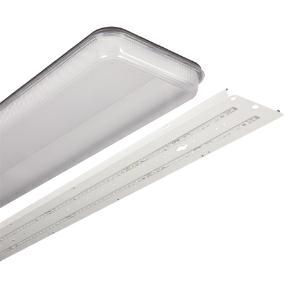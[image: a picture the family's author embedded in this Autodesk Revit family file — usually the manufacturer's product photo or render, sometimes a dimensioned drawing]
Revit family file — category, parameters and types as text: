
# Revit family: 3f_filippi_-_kit_led_retrofit_con_schermo_in_policarbonato_3f_filippi_-_a5027_-_kit_led_i3f_75__a3f_90___efdcafcb9e76d82e
name_source: partatom
category: Lighting Fixtures
units: mm (PartAtom-declared; Revit-internal decimal feet)

## family parameters
Cut with Voids When Loaded = No
Host = Face
Light Source = No
Part Type = Normal
Room Calculation Point = No
Round Connector Dimension = Use Diameter
Shared = No

## types (1)
- 3F Filippi - Kit LED Retrofit con schermo in policarbonato (1 x LED, 6996 lm, 49 W, 4000 K)
    Apparent Load = 49 VA
    Approval mark = ENEC
    CIE Flux Codes = 52 82 96 97 100
    Color Rendering = 80
    Color Temperature = 4000 K
    Control Gear = Electronic ballast
    Default Elevation = 1800 mm
    Description = Led retrofit kit suitable for Fluorescent Beta 2x i3F 75, A3F 90 and A3F 92 luminaires.

ILLUMINOTECHNICAL
Luminous efficiency 100% (DLOR 97%, ULOR 3%).
Initial luminous flux of the luminaire 6996 lm.
Symmetric distribution.
Installation Interdistance Transv.D = 1.27 x hu - Long.D = 1.26 x hu.
Tabular UGR (CIE 117 - 4H-8H; S=0.25H; 70/50/20): RUG 19.5 - 21.3.
Beam angle: 92° - 100°.
Luminous efficacy 143 lm/W.
Lifetime (L93/B10): 30000 h. (tq+25°C)
Lifetime (L90/B10): 50000 h. (tq+25°C)
Lifetime (L85/B10): 80000 h. (tq+25°C)
Lifetime (L80/B10): 100000 h. (tq+25°C)
Lifetime (L85/B10): 50000 h. (tq+35°C)
Sudden decreased luminous flux after 50000 hours: 0% (C0).
Photobiological safety in compliance with IEC/TR 62778: RG0 risk exempt, (IEC 62471).
In compliance with IEC/EN 62722-2-1 - IEC/EN 62717 standards.

SOURCE
2 linear LED modules 22W/840.
Energy efficiency class (UE 2019/2020 - UE 2019/2015): D.
CIE 13.3 Colour rendering index: CRI >80 (R9 <50%).
IES TM-30 Fidelity Index: Rf = 84 Rg = 95.
CCT nominal colour temperature 4000 K.
Colour initial tolerance (MacAdam): SDCM 3.

MECHANICAL
Diffuser in self-extinguishing V2 polycarbonate, photo-engraved interior, UV stabilised, injection moulded, with smooth outer surface, sealing gasket.
Gear-tray unit in hot-galvanised steel, painted in white polyester, fixed to the housing by means of "Ribloc" rapid devices in galvanised steel, hinged opening.
Luminaire with limited surface temperature. - D - (EN 60598-2-24)
Dimensions: 1565x235 mm, height 135 mm. Weight 2.93 kg.
Glow-wire test resistance 850°C.

ELECTRICAL
Halogen Free electronic wiring 230V-50/60Hz, power factor 0.97, THD <25%, constant output current, SELV, class I, 1 driver.
Power of the luminaire 49 W.
CE - IEC 60598-1 - EN 60598-1.
SAFE FLICKER: PstLM=<1 and SVM=<0.4 (IEC TR 61547-1 and IEC TR 63158), to ensure a more comfortable and safe light.
Luminaire compliant with EN 60598-2-22 for power supply from a centralised emergency system CPSS (Central Power Supply System), not incorporated in the luminaire - high risk areas excluded. The default power and flux are 100% in AC and 100% in DC.
Ambient temperature from -20°C to +35°C.
Temperature class T6 max 85°C.
Relative humidity UR: <85%.

INSTALLATION
Retrofit.
Correct installation of the retrofit LED kit, compliant with EN 60598-1 and CE marked, inside the 3F Filippi - Beta 2x i3F 75, A3F 90 and A3F 92 Fluorescent luminaires must be only performed by qualified personnel to ensure compliance with the national installation standards.
Attention: to maintain the degree of protection of the device and for the purposes of validity of the guarantee of the new retrofit kits, it is imperative to replace the old cable guides (on the body of the device) with the new ones supplied.
All accessories dedicated to this product are available on the Catalog and on our website www.3F-Filippi.com.

WARNING
Fixture not suitable for cold stores with an ambient temperature <0°C and/or relative humidity >85%.
Luminaire designed for disposal/recycling at end-of-life.
Replaceable (LED only) light source by a professional. Replaceable control gear by a professional.
    Height = 135 mm
    Lamp = 1 x LED
    Lamp Light Flux = 6996 lm
    Lamp Power = 49 W
    Lamp count = 1
    Length = 1565 mm
    Lifetime = 50000 h
    Luminous efficacy = 143 lm/W
    Manufacturer = 3F Filippi
    ModVariant = No
    Model = 3F Filippi - A5027 - Kit LED I3F 75, A3F 90, A3F 92-L1565 - 2X22W+PC
    Mounting Place = Ceiling
    Mounting Type = Surface mounted
    Number of Poles = 1
    OnlyDefault = Yes
    Power Factor = 1
    Product Name = 3F Filippi - Kit LED Retrofit con schermo in policarbonato
    Product group = ceiling mounted luminaire
    ProductGroupID = 3
    Protection Class = Protection class I
    Protection Degree = Degree of protection
    RLX_Detail_Level = 1
    RLX_Emergency_Light_Flux = 0 lm
    RLX_Emergency_Type = 0
    RLX_Emergency_Type_DB = No
    RlxData = <blob elided: 71957 chars, md5=da139dbd>
    Socket = socket
    Standby Power = 0 W
    System Light Flux = 6996 lm
    System Power = 49 W
    Type Comments = Product without accessories
    Type Image = 3ffilippi_a5027.jpg
    URL = http://relux.com
    VarID = ---
    Voltage = 0 V
    Weight = 0.00 kg
    Width = 235 mm

## geometry (parser evidence)
native form markers: Blend x4, Sweep x12
no freeform markers — native parametric forms only
